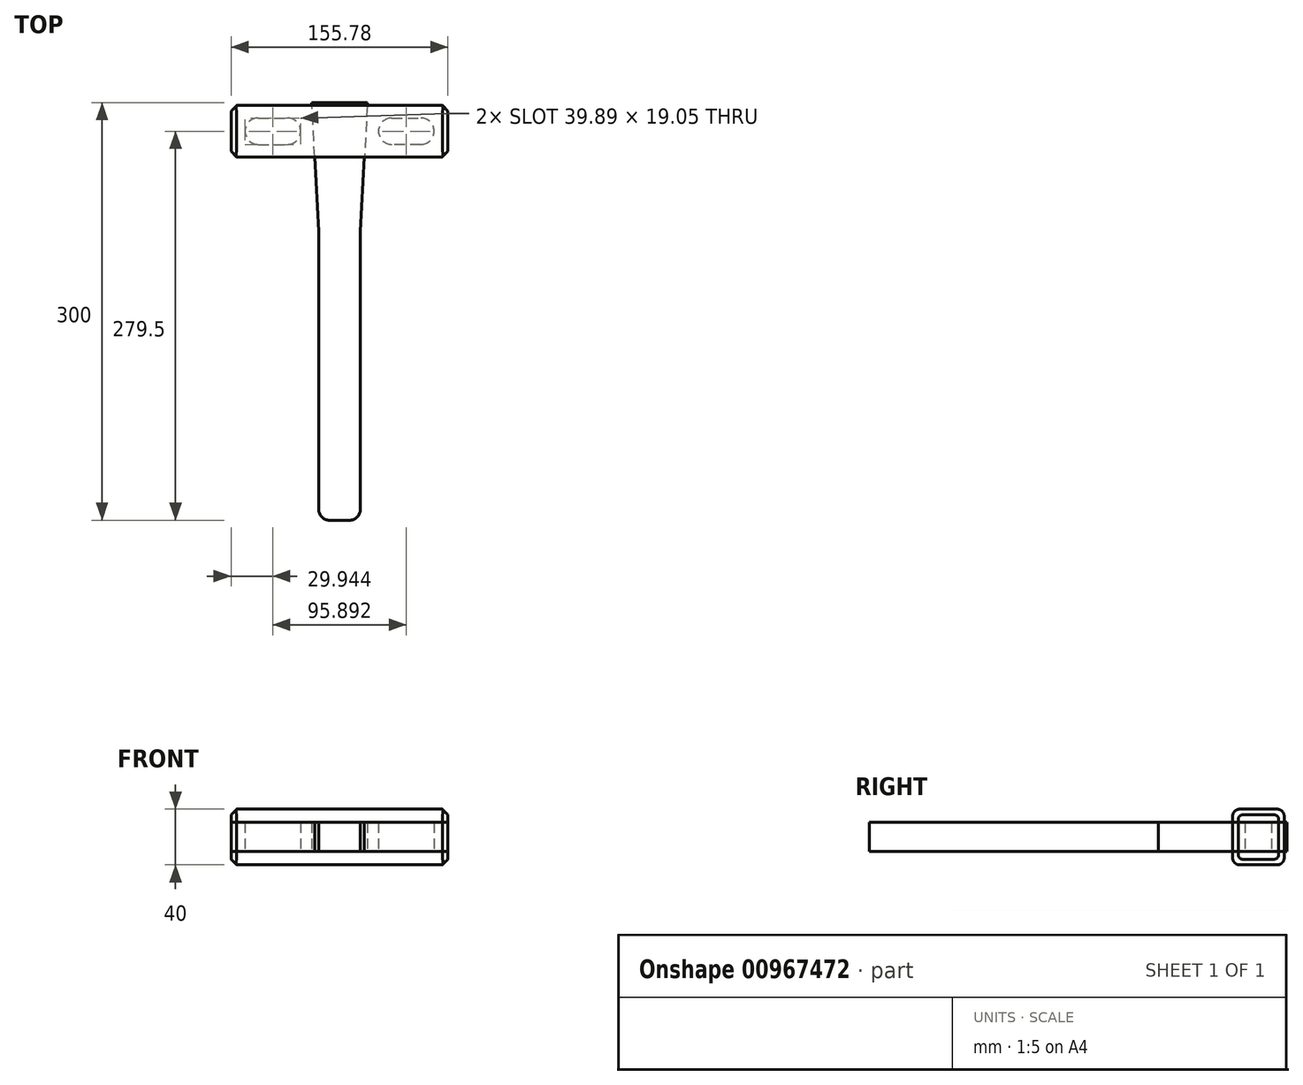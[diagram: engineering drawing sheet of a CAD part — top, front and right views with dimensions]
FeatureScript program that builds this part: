
annotation { "Feature Type Name" : "Feature", "Feature Type Description" : "" }
export const myFeature = defineFeature(function(context is Context, id is Id, definition is map)
    precondition{}
    {
        {
            var Q0;
            Q0=qCreatedBy(makeId("Top.planeOp"),FACE);
            var sketch = newSketch(context, id + "F0", { "sketchPlane" : qUnion([Q0])});
            skLineSegment(sketch, "E0.bottom", {"start": v(77.9, -18.5) * mm, "end": v(-77.9, -18.5) * mm});
            skLineSegment(sketch, "E0.top", {"start": v(77.9, 18.5) * mm, "end": v(-77.9, 18.5) * mm});
            skLineSegment(sketch, "E0.left", {"start": v(77.9, -18.5) * mm, "end": v(77.9, 18.5) * mm});
            skLineSegment(sketch, "E0.right", {"start": v(-77.9, -18.5) * mm, "end": v(-77.9, 18.5) * mm});
            skPoint(sketch, "E0.middle", {"position": v(0, 0) * mm});
            skArc(sketch, "E1", {"start": v(-58.37, 9.53) * mm, "mid": v(-67.9, 0) * mm, "end": v(-58.37, -9.53) * mm});
            skArc(sketch, "E2", {"start": v(-37.52, -9.53) * mm, "mid": v(-28, 0) * mm, "end": v(-37.52, 9.53) * mm});
            skArc(sketch, "E3", {"start": v(37.52, 9.53) * mm, "mid": v(28, 0) * mm, "end": v(37.52, -9.53) * mm});
            skArc(sketch, "E4", {"start": v(58.37, -9.53) * mm, "mid": v(67.9, 0) * mm, "end": v(58.37, 9.53) * mm});
            skLineSegment(sketch, "E5", {"start": v(-58.37, 9.53) * mm, "end": v(-37.52, 9.53) * mm});
            skLineSegment(sketch, "E6", {"start": v(-58.37, -9.53) * mm, "end": v(-37.52, -9.53) * mm});
            skLineSegment(sketch, "E7", {"start": v(37.52, 9.53) * mm, "end": v(58.37, 9.53) * mm});
            skLineSegment(sketch, "E8", {"start": v(58.37, -9.52) * mm, "end": v(37.52, -9.53) * mm});
            skLineSegment(sketch, "E9", {"start": v(-67.9, 0) * mm, "end": v(-77.9, 0) * mm, "construction": true});
            skLineSegment(sketch, "E10", {"start": v(77.9, 0) * mm, "end": v(67.9, 0) * mm, "construction": true});
            skLineSegment(sketch, "E11", {"start": v(-28, 0) * mm, "end": v(-20, 0) * mm, "construction": true});
            skLineSegment(sketch, "E12", {"start": v(28, 0) * mm, "end": v(20, 0) * mm, "construction": true});
            skLineSegment(sketch, "E13", {"start": v(-20, 20.5) * mm, "end": v(20, 20.5) * mm});
            skPoint(sketch, "E14", {"position": v(0, 20.5) * mm});
            skLineSegment(sketch, "E15", {"start": v(20, 20.5) * mm, "end": v(15, -72) * mm});
            skLineSegment(sketch, "E16", {"start": v(15, -72) * mm, "end": v(-15, -72) * mm, "construction": true});
            skLineSegment(sketch, "E17", {"start": v(-15, -72) * mm, "end": v(-20, 20.5) * mm});
            skPoint(sketch, "E18", {"position": v(0, -72) * mm});
            skLineSegment(sketch, "E19", {"start": v(20, 20.5) * mm, "end": v(20, -72) * mm, "construction": true});
            skLineSegment(sketch, "E20", {"start": v(20, -72) * mm, "end": v(15, -72) * mm, "construction": true});
            skLineSegment(sketch, "E21", {"start": v(-20, 20.5) * mm, "end": v(-20, -72) * mm, "construction": true});
            skLineSegment(sketch, "E22", {"start": v(-20, -72) * mm, "end": v(-15, -72) * mm, "construction": true});
            skLineSegment(sketch, "E23", {"start": v(15, -72) * mm, "end": v(15, -279.5) * mm});
            skLineSegment(sketch, "E24", {"start": v(15, -279.5) * mm, "end": v(-15, -279.5) * mm});
            skLineSegment(sketch, "E25", {"start": v(-15, -279.5) * mm, "end": v(-15, -72) * mm});
            skPoint(sketch, "E26", {"position": v(-17.9, -18.5) * mm});
            skPoint(sketch, "E27", {"position": v(-19.9, 18.5) * mm});
            skSolve(sketch);
        }
        {
            var Q0;
            {var subQ0=sQuery(id+"F0.wireOp",EDGE,"E15");var subQ1=sQuery(id+"F0.wireOp",EDGE,"E0.bottom");var subQ2=makeQuery(id+"F0.imprint","INTERSECT",VERTEX,{"derivedFrom":[subQ1,subQ0]});Q0=makeQuery(id+"F0.imprint","IMPRINT",FACE,{"disambiguationData":[TD([[makeQuery(id+"F0.imprint","IMPRINT",EDGE,{"disambiguationData":[TD([[subQ2,-1.0]])],"derivedFrom":subQ1}),-1.0]])]});}
            var Q1;
            {var subQ0=sQuery(id+"F0.wireOp",EDGE,"E23");Q1=makeQuery(id+"F0.imprint","IMPRINT",FACE,{"disambiguationData":[TD([[makeQuery(id+"F0.imprint","IMPRINT",EDGE,{"derivedFrom":subQ0}),-1.0]])]});}
            var Q2;
            {var subQ5=sQuery(id+"F0.wireOp",EDGE,"E13");Q2=makeQuery(id+"F0.imprint","IMPRINT",FACE,{"disambiguationData":[TD([[makeQuery(id+"F0.imprint","IMPRINT",EDGE,{"derivedFrom":subQ5}),-1.0]])]});}
            var Q3;
            {var subQ0=sQuery(id+"F0.wireOp",EDGE,"4JOdfxkb-PHg7-tYiD-hHk8-InOCBoPfvKoK");Q3=makeQuery(id+"F0.imprint","IMPRINT",FACE,{"disambiguationData":[TD([[makeQuery(id+"F0.imprint","IMPRINT",EDGE,{"derivedFrom":subQ0}),-1.0]])]});}
            var Q4;
            {var subQ2=sQuery(id+"F0.wireOp",EDGE,"kALUJpjO-avBj-7vEE-N3Md-RMGskx6gLwWT");Q4=makeQuery(id+"F0.imprint","IMPRINT",FACE,{"disambiguationData":[TD([[makeQuery(id+"F0.imprint","IMPRINT",EDGE,{"derivedFrom":subQ2}),-1.0]])]});}
            var Q5;
            {var subQ0=sQuery(id+"F0.wireOp",EDGE,"E15");var subQ1=sQuery(id+"F0.wireOp",EDGE,"E0.bottom");var subQ2=makeQuery(id+"F0.imprint","INTERSECT",VERTEX,{"derivedFrom":[subQ1,subQ0]});Q5=makeQuery(id+"F0.imprint","IMPRINT",FACE,{"disambiguationData":[TD([[makeQuery(id+"F0.imprint","IMPRINT",EDGE,{"disambiguationData":[TD([[subQ2,-1.0]])],"derivedFrom":subQ1}),1.0]])]});}
            extrude(context, id + "F1", {"entities" : qUnion([Q0, Q1, Q2, Q3, Q4, Q5]), "depth" : 21 * mm, "offsetDistance" : 25 * mm});
        }
        {
            var Q0;
            {var subQ5=sQuery(id+"F0.wireOp",EDGE,"E0.right");Q0=makeQuery(id+"F0.imprint","IMPRINT",FACE,{"disambiguationData":[TD([[makeQuery(id+"F0.imprint","IMPRINT",EDGE,{"derivedFrom":subQ5}),-1.0]])]});}
            var Q1;
            {var subQ5=sQuery(id+"F0.wireOp",EDGE,"E0.left");Q1=makeQuery(id+"F0.imprint","IMPRINT",FACE,{"disambiguationData":[TD([[makeQuery(id+"F0.imprint","IMPRINT",EDGE,{"derivedFrom":subQ5}),1.0]])]});}
            extrude(context, id + "F2", {"entities" : qUnion([Q0, Q1]), "depth" : 21 * mm, "offsetDistance" : 25 * mm});
        }
        {
            var Q0;
            {var subQ0=sQuery(id+"F0.wireOp",EDGE,"E0.right");Q0=makeQuery(id+"F0.imprint","IMPRINT",FACE,{"disambiguationData":[TD([[makeQuery(id+"F0.imprint","IMPRINT",EDGE,{"derivedFrom":subQ0}),-1.0]])]});}
            var Q1;
            Q1=makeQuery(id+"F0.imprint","IMPRINT",FACE,{"disambiguationData":[TD([[makeQuery(id+"F0.imprint","IMPRINT",EDGE,{"derivedFrom":sQuery(id+"F0.wireOp",EDGE,"E1")}),1.0]])]});
            var Q2;
            {var subQ0=sQuery(id+"F0.wireOp",EDGE,"E15");var subQ1=sQuery(id+"F0.wireOp",EDGE,"E0.bottom");var subQ2=makeQuery(id+"F0.imprint","INTERSECT",VERTEX,{"derivedFrom":[subQ1,subQ0]});Q2=makeQuery(id+"F0.imprint","IMPRINT",FACE,{"disambiguationData":[TD([[makeQuery(id+"F0.imprint","IMPRINT",EDGE,{"disambiguationData":[TD([[subQ2,-1.0]])],"derivedFrom":subQ1}),-1.0]])]});}
            var Q3;
            {var subQ0=sQuery(id+"F0.wireOp",EDGE,"E0.left");Q3=makeQuery(id+"F0.imprint","IMPRINT",FACE,{"disambiguationData":[TD([[makeQuery(id+"F0.imprint","IMPRINT",EDGE,{"derivedFrom":subQ0}),1.0]])]});}
            var Q4;
            Q4=makeQuery(id+"F0.imprint","IMPRINT",FACE,{"disambiguationData":[TD([[makeQuery(id+"F0.imprint","IMPRINT",EDGE,{"derivedFrom":sQuery(id+"F0.wireOp",EDGE,"E3")}),1.0]])]});
            extrude(context, id + "F3", {"entities" : qUnion([Q0, Q1, Q2, Q3, Q4]), "oppositeDirection" : true, "depth" : 9.5 * mm, "offsetDistance" : 25 * mm});
        }
        {
            var Q0;
            Q0=makeQuery(id+"F2.opExtrude","SWEPT_EDGE",EDGE,{"disambiguationData":[OSD([sQuery(id+"F0.wireOp",EDGE,"E0.top"),sQuery(id+"F0.wireOp",EDGE,"E0.left")])]});
            cPoint(context, id + "F4", {"entities" : qUnion([Q0]), "parameter" : 0.5});
        }
        {
            var Q0;
            Q0 = qCreatedBy(id + "F4" ,VERTEX);
            var Q1;
            Q1=makeQuery(id+"F2.opExtrude","SWEPT_EDGE",EDGE,{"disambiguationData":[OSD([sQuery(id+"F0.wireOp",EDGE,"E0.top"),sQuery(id+"F0.wireOp",EDGE,"E0.left")])]});
            cPlane(context, id + "F5", {"entities" : qUnion([Q0, Q1]), "cplaneType" : CPlaneType.LINE_POINT, "offset" : 25 * mm, "width" : 150 * mm, "height" : 150 * mm});
        }
        {
            var Q0;
            Q0=makeQuery(id+"F3.opExtrude","SWEPT_BODY",BODY,{"disambiguationData":[OSD([sQuery(id+"F0.wireOp",EDGE,"E0.bottom"),sQuery(id+"F0.wireOp",EDGE,"E0.top"),sQuery(id+"F0.wireOp",EDGE,"E0.left"),sQuery(id+"F0.wireOp",EDGE,"E0.right"),sQuery(id+"F0.wireOp",EDGE,"BJWi1EpR-n2ml-vamB-hSDR-3Px4BMayj7m5.bottom")])]});
            var Q1;
            Q1=qCreatedBy(id+"F5.planeOp",FACE);
            mirror(context, id + "F6", {"entities" : qUnion([Q0]), "mirrorPlane" : qUnion([Q1])});
        }
        {
            var Q0;
            Q0=makeQuery(id+"F1.opExtrude","SWEPT_EDGE",EDGE,{"disambiguationData":[OSD([sQuery(id+"F0.wireOp",EDGE,"E24"),sQuery(id+"F0.wireOp",EDGE,"E25")])]});
            var Q1;
            Q1=makeQuery(id+"F1.opExtrude","SWEPT_EDGE",EDGE,{"disambiguationData":[OSD([sQuery(id+"F0.wireOp",EDGE,"E23"),sQuery(id+"F0.wireOp",EDGE,"E24")])]});
            fillet(context, id + "F7", {"entities" : qUnion([Q0, Q1]), "radius" : 8 * mm, "allowEdgeOverflow" : false});
        }
        {
            var Q0;
            Q0=makeQuery(id+"F6.opPattern","COPY",EDGE,{"derivedFrom":makeQuery(id+"F3.opExtrude","CAP_EDGE",EDGE,{"disambiguationData":[OSD([sQuery(id+"F0.wireOp",EDGE,"E0.left")])],"isStart":false}),"instanceName":"1"});
            var Q1;
            Q1=makeQuery(id+"F3.opExtrude","CAP_EDGE",EDGE,{"disambiguationData":[OSD([sQuery(id+"F0.wireOp",EDGE,"E0.left")])],"isStart":false});
            var Q2;
            Q2=makeQuery(id+"F6.opPattern","COPY",EDGE,{"derivedFrom":makeQuery(id+"F3.opExtrude","SWEPT_EDGE",EDGE,{"disambiguationData":[OSD([sQuery(id+"F0.wireOp",EDGE,"E0.top"),sQuery(id+"F0.wireOp",EDGE,"E0.left")])]}),"instanceName":"1"});
            var Q3;
            Q3=makeQuery(id+"F2.opExtrude","SWEPT_EDGE",EDGE,{"disambiguationData":[OSD([sQuery(id+"F0.wireOp",EDGE,"E0.top"),sQuery(id+"F0.wireOp",EDGE,"E0.left")])]});
            var Q4;
            Q4=makeQuery(id+"F3.opExtrude","SWEPT_EDGE",EDGE,{"disambiguationData":[OSD([sQuery(id+"F0.wireOp",EDGE,"E0.top"),sQuery(id+"F0.wireOp",EDGE,"E0.left")])]});
            var Q5;
            Q5=makeQuery(id+"F6.opPattern","COPY",EDGE,{"derivedFrom":makeQuery(id+"F3.opExtrude","SWEPT_EDGE",EDGE,{"disambiguationData":[OSD([sQuery(id+"F0.wireOp",EDGE,"E0.bottom"),sQuery(id+"F0.wireOp",EDGE,"E0.left")])]}),"instanceName":"1"});
            var Q6;
            Q6=makeQuery(id+"F2.opExtrude","SWEPT_EDGE",EDGE,{"disambiguationData":[OSD([sQuery(id+"F0.wireOp",EDGE,"E0.bottom"),sQuery(id+"F0.wireOp",EDGE,"E0.left")])]});
            var Q7;
            Q7=makeQuery(id+"F3.opExtrude","SWEPT_EDGE",EDGE,{"disambiguationData":[OSD([sQuery(id+"F0.wireOp",EDGE,"E0.bottom"),sQuery(id+"F0.wireOp",EDGE,"E0.left")])]});
            var Q8;
            Q8=makeQuery(id+"F3.opExtrude","SWEPT_EDGE",EDGE,{"disambiguationData":[OSD([sQuery(id+"F0.wireOp",EDGE,"E0.top"),sQuery(id+"F0.wireOp",EDGE,"E0.right")])]});
            var Q9;
            Q9=makeQuery(id+"F2.opExtrude","SWEPT_EDGE",EDGE,{"disambiguationData":[OSD([sQuery(id+"F0.wireOp",EDGE,"E0.top"),sQuery(id+"F0.wireOp",EDGE,"E0.right")])]});
            var Q10;
            Q10=makeQuery(id+"F6.opPattern","COPY",EDGE,{"derivedFrom":makeQuery(id+"F3.opExtrude","SWEPT_EDGE",EDGE,{"disambiguationData":[OSD([sQuery(id+"F0.wireOp",EDGE,"E0.top"),sQuery(id+"F0.wireOp",EDGE,"E0.right")])]}),"instanceName":"1"});
            var Q11;
            Q11=makeQuery(id+"F6.opPattern","COPY",EDGE,{"derivedFrom":makeQuery(id+"F3.opExtrude","CAP_EDGE",EDGE,{"disambiguationData":[OSD([sQuery(id+"F0.wireOp",EDGE,"E0.right")])],"isStart":false}),"instanceName":"1"});
            var Q12;
            Q12=makeQuery(id+"F6.opPattern","COPY",EDGE,{"derivedFrom":makeQuery(id+"F3.opExtrude","SWEPT_EDGE",EDGE,{"disambiguationData":[OSD([sQuery(id+"F0.wireOp",EDGE,"E0.bottom"),sQuery(id+"F0.wireOp",EDGE,"E0.right")])]}),"instanceName":"1"});
            var Q13;
            Q13=makeQuery(id+"F2.opExtrude","SWEPT_EDGE",EDGE,{"disambiguationData":[OSD([sQuery(id+"F0.wireOp",EDGE,"E0.bottom"),sQuery(id+"F0.wireOp",EDGE,"E0.right")])]});
            var Q14;
            Q14=makeQuery(id+"F3.opExtrude","SWEPT_EDGE",EDGE,{"disambiguationData":[OSD([sQuery(id+"F0.wireOp",EDGE,"E0.bottom"),sQuery(id+"F0.wireOp",EDGE,"E0.right")])]});
            var Q15;
            Q15=makeQuery(id+"F3.opExtrude","CAP_EDGE",EDGE,{"disambiguationData":[OSD([sQuery(id+"F0.wireOp",EDGE,"E0.right")])],"isStart":false});
            chamfer(context, id + "F8", {"entities" : qUnion([Q0, Q1, Q2, Q3, Q4, Q5, Q6, Q7, Q8, Q9, Q10, Q11, Q12, Q13, Q14, Q15]), "width" : 4 * mm, "tangentPropagation" : true});
        }
        {
            var Q0;
            Q0=makeQuery(id+"F6.opPattern","COPY",EDGE,{"derivedFrom":makeQuery(id+"F3.opExtrude","CAP_EDGE",EDGE,{"disambiguationData":[OSD([sQuery(id+"F0.wireOp",EDGE,"E0.bottom")])],"isStart":false}),"instanceName":"1"});
            var Q1;
            Q1=makeQuery(id+"F6.opPattern","COPY",EDGE,{"derivedFrom":makeQuery(id+"F3.opExtrude","CAP_EDGE",EDGE,{"disambiguationData":[OSD([sQuery(id+"F0.wireOp",EDGE,"E0.top")])],"isStart":false}),"instanceName":"1"});
            var Q2;
            Q2=makeQuery(id+"F3.opExtrude","CAP_EDGE",EDGE,{"disambiguationData":[OSD([sQuery(id+"F0.wireOp",EDGE,"E0.bottom")])],"isStart":false});
            var Q3;
            Q3=makeQuery(id+"F3.opExtrude","CAP_EDGE",EDGE,{"disambiguationData":[OSD([sQuery(id+"F0.wireOp",EDGE,"E0.top")])],"isStart":false});
            var Q4;
            {var subQ0=sQuery(id+"F0.wireOp",EDGE,"E0.left");Q4=makeQuery(id+"F8.opChamfer","BLEND_EDGE",EDGE,{"blendedFrom":[makeQuery(id+"F6.opPattern","COPY",EDGE,{"derivedFrom":makeQuery(id+"F3.opExtrude","SWEPT_EDGE",EDGE,{"disambiguationData":[OSD([sQuery(id+"F0.wireOp",EDGE,"E0.bottom"),subQ0])]}),"instanceName":"1"}),makeQuery(id+"F6.opPattern","COPY",EDGE,{"derivedFrom":makeQuery(id+"F3.opExtrude","CAP_EDGE",EDGE,{"disambiguationData":[OSD([subQ0])],"isStart":false}),"instanceName":"1"})],"blendedInto":[]});}
            var Q5;
            {var subQ0=sQuery(id+"F0.wireOp",EDGE,"E0.left");Q5=makeQuery(id+"F8.opChamfer","BLEND_EDGE",EDGE,{"blendedFrom":[makeQuery(id+"F6.opPattern","COPY",EDGE,{"derivedFrom":makeQuery(id+"F3.opExtrude","SWEPT_EDGE",EDGE,{"disambiguationData":[OSD([sQuery(id+"F0.wireOp",EDGE,"E0.top"),subQ0])]}),"instanceName":"1"}),makeQuery(id+"F6.opPattern","COPY",EDGE,{"derivedFrom":makeQuery(id+"F3.opExtrude","CAP_EDGE",EDGE,{"disambiguationData":[OSD([subQ0])],"isStart":false}),"instanceName":"1"})],"blendedInto":[]});}
            var Q6;
            {var subQ0=sQuery(id+"F0.wireOp",EDGE,"E0.left");Q6=makeQuery(id+"F8.opChamfer","BLEND_EDGE",EDGE,{"blendedFrom":[makeQuery(id+"F3.opExtrude","SWEPT_EDGE",EDGE,{"disambiguationData":[OSD([sQuery(id+"F0.wireOp",EDGE,"E0.bottom"),subQ0])]}),makeQuery(id+"F3.opExtrude","CAP_EDGE",EDGE,{"disambiguationData":[OSD([subQ0])],"isStart":false})],"blendedInto":[]});}
            var Q7;
            {var subQ0=sQuery(id+"F0.wireOp",EDGE,"E0.left");Q7=makeQuery(id+"F8.opChamfer","BLEND_EDGE",EDGE,{"blendedFrom":[makeQuery(id+"F3.opExtrude","SWEPT_EDGE",EDGE,{"disambiguationData":[OSD([sQuery(id+"F0.wireOp",EDGE,"E0.top"),subQ0])]}),makeQuery(id+"F3.opExtrude","CAP_EDGE",EDGE,{"disambiguationData":[OSD([subQ0])],"isStart":false})],"blendedInto":[]});}
            var Q8;
            {var subQ0=sQuery(id+"F0.wireOp",EDGE,"E0.right");Q8=makeQuery(id+"F8.opChamfer","BLEND_EDGE",EDGE,{"blendedFrom":[makeQuery(id+"F3.opExtrude","SWEPT_EDGE",EDGE,{"disambiguationData":[OSD([sQuery(id+"F0.wireOp",EDGE,"E0.top"),subQ0])]}),makeQuery(id+"F3.opExtrude","CAP_EDGE",EDGE,{"disambiguationData":[OSD([subQ0])],"isStart":false})],"blendedInto":[]});}
            var Q9;
            {var subQ0=sQuery(id+"F0.wireOp",EDGE,"E0.right");Q9=makeQuery(id+"F8.opChamfer","BLEND_EDGE",EDGE,{"blendedFrom":[makeQuery(id+"F3.opExtrude","SWEPT_EDGE",EDGE,{"disambiguationData":[OSD([sQuery(id+"F0.wireOp",EDGE,"E0.bottom"),subQ0])]}),makeQuery(id+"F3.opExtrude","CAP_EDGE",EDGE,{"disambiguationData":[OSD([subQ0])],"isStart":false})],"blendedInto":[]});}
            var Q10;
            {var subQ0=sQuery(id+"F0.wireOp",EDGE,"E0.right");Q10=makeQuery(id+"F8.opChamfer","BLEND_EDGE",EDGE,{"blendedFrom":[makeQuery(id+"F6.opPattern","COPY",EDGE,{"derivedFrom":makeQuery(id+"F3.opExtrude","SWEPT_EDGE",EDGE,{"disambiguationData":[OSD([sQuery(id+"F0.wireOp",EDGE,"E0.top"),subQ0])]}),"instanceName":"1"}),makeQuery(id+"F6.opPattern","COPY",EDGE,{"derivedFrom":makeQuery(id+"F3.opExtrude","CAP_EDGE",EDGE,{"disambiguationData":[OSD([subQ0])],"isStart":false}),"instanceName":"1"})],"blendedInto":[]});}
            var Q11;
            {var subQ0=sQuery(id+"F0.wireOp",EDGE,"E0.right");Q11=makeQuery(id+"F8.opChamfer","BLEND_EDGE",EDGE,{"blendedFrom":[makeQuery(id+"F6.opPattern","COPY",EDGE,{"derivedFrom":makeQuery(id+"F3.opExtrude","SWEPT_EDGE",EDGE,{"disambiguationData":[OSD([sQuery(id+"F0.wireOp",EDGE,"E0.bottom"),subQ0])]}),"instanceName":"1"}),makeQuery(id+"F6.opPattern","COPY",EDGE,{"derivedFrom":makeQuery(id+"F3.opExtrude","CAP_EDGE",EDGE,{"disambiguationData":[OSD([subQ0])],"isStart":false}),"instanceName":"1"})],"blendedInto":[]});}
            fillet(context, id + "F9", {"entities" : qUnion([Q0, Q1, Q2, Q3, Q4, Q5, Q6, Q7, Q8, Q9, Q10, Q11]), "radius" : 5 * mm, "tangentPropagation" : true, "allowEdgeOverflow" : false});
        }
    });
